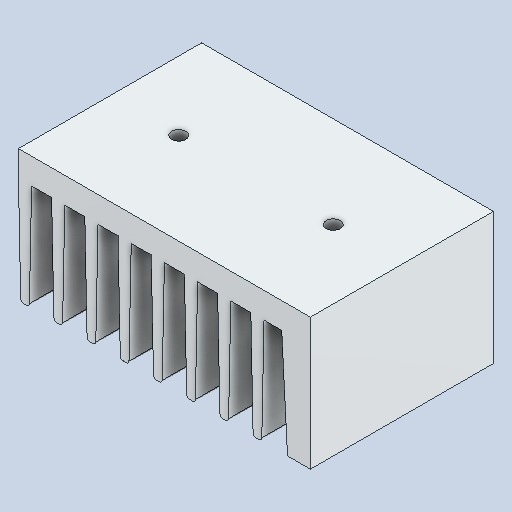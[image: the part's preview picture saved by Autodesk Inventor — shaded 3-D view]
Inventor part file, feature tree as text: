
AUTODESK INVENTOR PART (.ipt)
format: ipt  version: 2023.1 (Build 271208000, 208)  size: 143,872 bytes
history: native  units: in
note: dims shown in document units (in); Inventor stores cm internally (conversion verified against a paired STEP export)
features: mirror x1
ambient origin geometry x8: Origin, YZ Plane, XZ Plane, XY Plane, X Axis, Y Axis, Z Axis, Center Point
bodies: Solid1 (feature_tree)
feature tree (1):
  mirror  "Mirror1"
